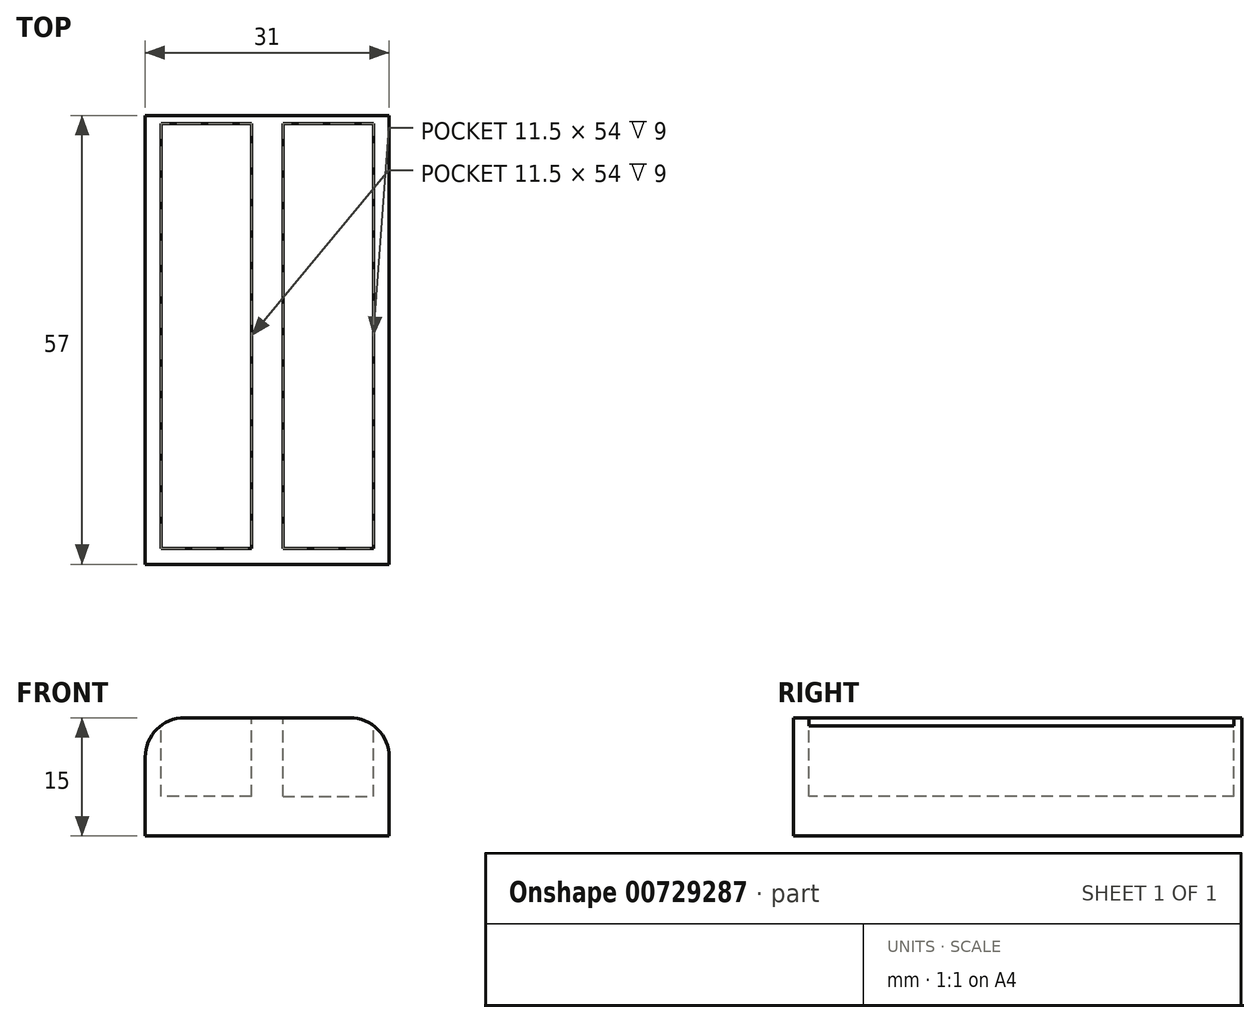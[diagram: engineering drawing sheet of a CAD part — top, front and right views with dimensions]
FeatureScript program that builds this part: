
annotation { "Feature Type Name" : "Feature", "Feature Type Description" : "" }
export const myFeature = defineFeature(function(context is Context, id is Id, definition is map)
    precondition{}
    {
        {
            var Q0;
            Q0=qCreatedBy(makeId("Top.planeOp"),FACE);
            var sketch = newSketch(context, id + "F0", { "sketchPlane" : qUnion([Q0])});
            skLineSegment(sketch, "E0.bottom", {"start": v(-15.5, 28.5) * mm, "end": v(15.5, 28.5) * mm});
            skLineSegment(sketch, "E0.top", {"start": v(-15.5, -28.5) * mm, "end": v(15.5, -28.5) * mm});
            skLineSegment(sketch, "E0.left", {"start": v(-15.5, 28.5) * mm, "end": v(-15.5, -28.5) * mm});
            skLineSegment(sketch, "E0.right", {"start": v(15.5, 28.5) * mm, "end": v(15.5, -28.5) * mm});
            skPoint(sketch, "E0.middle", {"position": v(0, 0) * mm});
            skSolve(sketch);
        }
        {
            var Q0;
            Q0 = qSketchRegion(id + "F0", true);
            extrude(context, id + "F1", {"entities" : qUnion([Q0]), "depth" : 15 * mm, "offsetDistance" : 25 * mm});
        }
        {
            var Q0;
            Q0=makeQuery(id+"F1.opExtrude","CAP_EDGE",EDGE,{"disambiguationData":[OSD([sQuery(id+"F0.wireOp",EDGE,"E0.right")])],"isStart":false});
            var Q1;
            Q1=makeQuery(id+"F1.opExtrude","CAP_EDGE",EDGE,{"disambiguationData":[OSD([sQuery(id+"F0.wireOp",EDGE,"E0.left")])],"isStart":false});
            fillet(context, id + "F2", {"entities" : qUnion([Q0, Q1]), "radius" : 5 * mm, "tangentPropagation" : true, "allowEdgeOverflow" : false});
        }
        {
            var Q0;
            Q0=makeQuery(id+"F1.opExtrude","CAP_FACE",FACE,{"disambiguationData":[OSD([sQuery(id+"F0.wireOp",EDGE,"E0.bottom"),sQuery(id+"F0.wireOp",EDGE,"E0.top"),sQuery(id+"F0.wireOp",EDGE,"E0.left"),sQuery(id+"F0.wireOp",EDGE,"E0.right")])],"isStart":false});
            var sketch = newSketch(context, id + "F3", { "sketchPlane" : qUnion([Q0])});
            skLineSegment(sketch, "E1.bottom", {"start": v(2, 27.5) * mm, "end": v(13.5, 27.5) * mm});
            skLineSegment(sketch, "E1.top", {"start": v(2, -26.5) * mm, "end": v(13.5, -26.5) * mm});
            skLineSegment(sketch, "E1.left", {"start": v(2, 27.5) * mm, "end": v(2, -26.5) * mm});
            skLineSegment(sketch, "E1.right", {"start": v(13.5, 27.5) * mm, "end": v(13.5, -26.5) * mm});
            skLineSegment(sketch, "E2.MirrorCS", {"start": v(-2, 27.5) * mm, "end": v(-13.5, 27.5) * mm});
            skLineSegment(sketch, "E3.MirrorCS", {"start": v(-2, -26.5) * mm, "end": v(-13.5, -26.5) * mm});
            skLineSegment(sketch, "E4.MirrorCS", {"start": v(-2, 27.5) * mm, "end": v(-2, -26.5) * mm});
            skLineSegment(sketch, "E5.MirrorCS", {"start": v(-13.5, 27.5) * mm, "end": v(-13.5, -26.5) * mm});
            skSolve(sketch);
        }
        {
            var Q0;
            Q0 = qSketchRegion(id + "F3", true);
            extrude(context, id + "F4", {"entities" : qUnion([Q0]), "operationType" : NewBodyOperationType.REMOVE, "oppositeDirection" : true, "depth" : 10 * mm, "offsetDistance" : 25 * mm});
        }
    });
